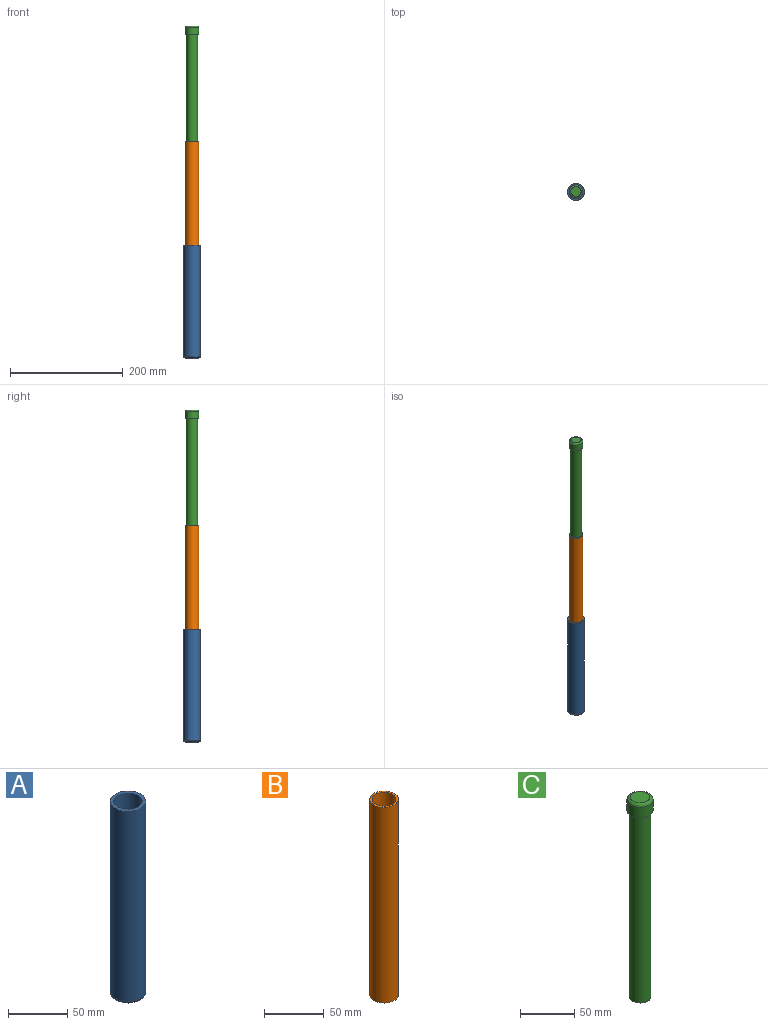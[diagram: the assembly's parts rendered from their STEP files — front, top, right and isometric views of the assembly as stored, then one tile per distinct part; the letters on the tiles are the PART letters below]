
ASSEMBLY  parts=3 mates=2
PART A: 6 faces, bbox 32.5x32.5x200 mm
  f0: cylinder r=15mm len=197mm, axis (0,0,-1), area 18566.8mm2, adj f3,f5
  f1: plane 24x24mm, normal (0,0,-1), area 452.4mm2, adj f5
  f2: cylinder r=12mm len=190mm, axis (0,0,-1), area 14325.7mm2, adj f3,f4
  f3: plane 30x30mm, normal (0,0,1), area 254.5mm2, adj f0,f2
  f4: plane 24x24mm, normal (0,0,1), area 452.4mm2, adj f2
  f5: torus R=12mm, axis (0,0,1), area 411.9mm2, adj f0,f1
PART B: 4 faces, bbox 24x24x200 mm
  f0: cylinder r=10mm len=200mm, axis (0,0,-1), area 12566.4mm2, adj f2,f3
  f1: cylinder r=12mm len=200mm, axis (0,0,-1), area 15079.6mm2, adj f2,f3
  f2: plane 24x24mm, normal (0,0,1), area 138.2mm2, adj f0,f1
  f3: plane 24x24mm, normal (0,0,-1), area 138.2mm2, adj f0,f1
PART C: 8 faces, bbox 26x26x225 mm
  f0: cylinder r=8mm len=210mm, axis (0,0,-1), area 10555.8mm2, adj f2,f6
  f1: cylinder r=10mm len=210mm, axis (0,0,-1), area 13194.7mm2, adj f2,f3
  f2: plane 20x20mm, normal (0,0,-1), area 113.1mm2, adj f0,f1
  f3: plane 24x24mm, normal (0,0,-1), area 138.2mm2, adj f1,f5
  f4: plane 18x18mm, normal (0,0,1), area 254.5mm2, adj f7
  f5: cylinder r=12mm len=24mm, axis (0,0,-1), area 904.8mm2, adj f3,f7
  f6: plane 16x16mm, normal (0,0,-1), area 201.1mm2, adj f0
  f7: torus R=9mm, axis (0,0,1), area 323mm2, adj f4,f5
PLACE A at identity fixed
PLACE B t=(0,0,173)mm
PLACE C t=(0,0,353)mm
MATE slider C.f0 <-> A.f0  axis (0,0,-1) through (0,0,363)mm
MATE slider B.f1 <-> A.f0  axis (0,0,-1) through (0,0,183)mm
